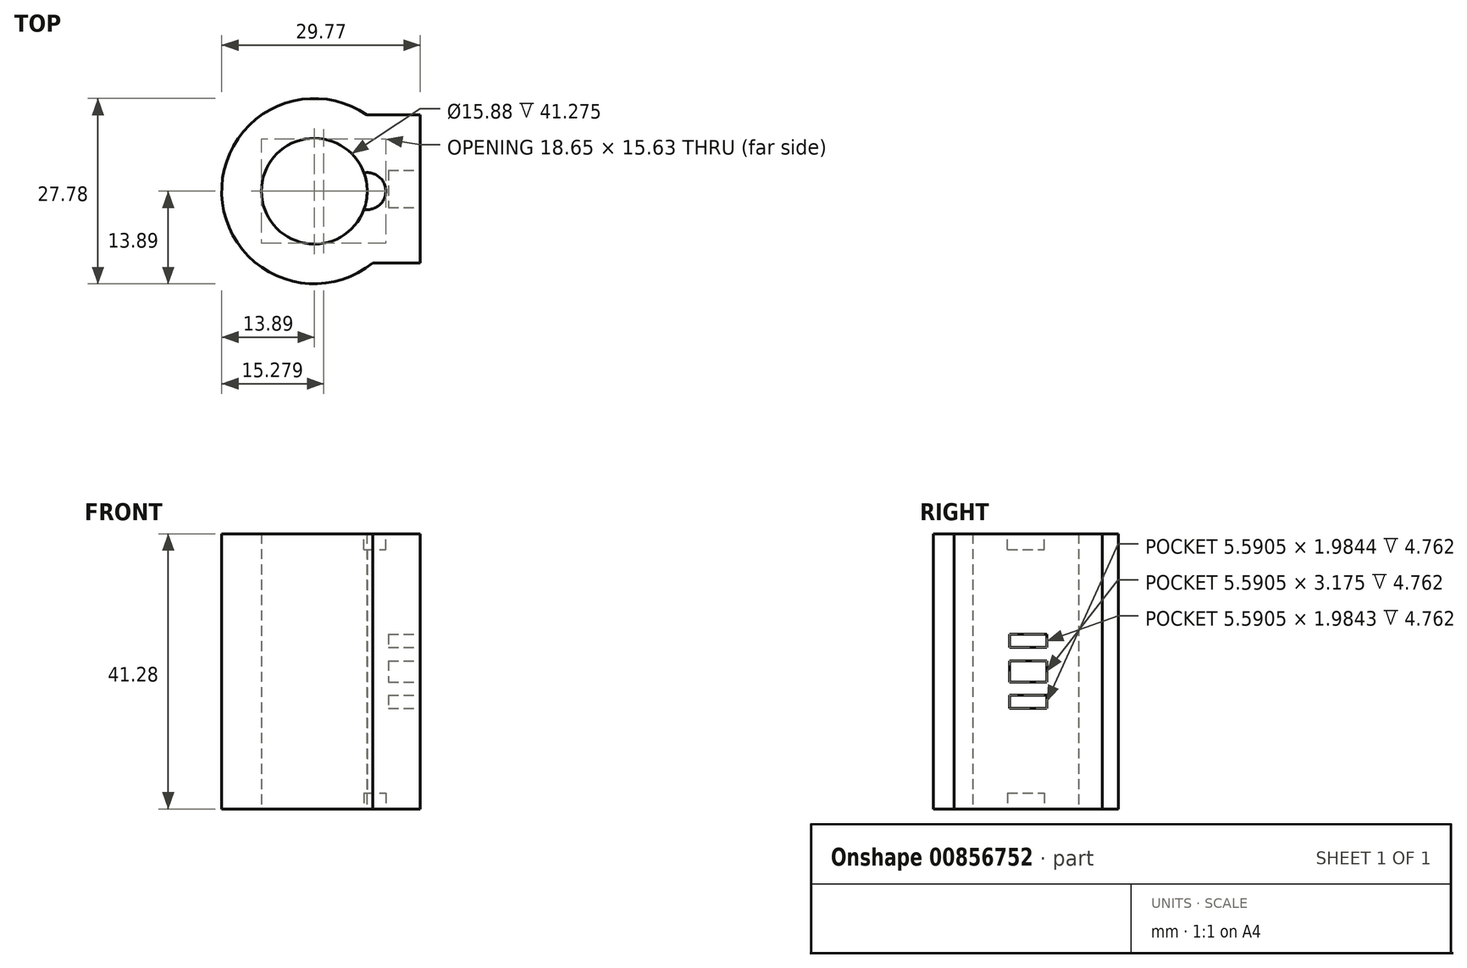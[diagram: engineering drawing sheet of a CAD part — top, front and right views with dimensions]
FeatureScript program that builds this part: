
annotation { "Feature Type Name" : "Feature", "Feature Type Description" : "" }
export const myFeature = defineFeature(function(context is Context, id is Id, definition is map)
    precondition{}
    {
        {
            var Q0;
            Q0=qCreatedBy(makeId("Top.planeOp"),FACE);
            var sketch = newSketch(context, id + "F0", { "sketchPlane" : qUnion([Q0])});
            skCircle(sketch, "E0", {"center": v(0, 0) * mm, "radius": 13.9 * mm});
            skCircle(sketch, "E1", {"center": v(0, 0) * mm, "radius": 7.94 * mm});
            skLineSegment(sketch, "E2", {"start": v(7.88, 11.44) * mm, "end": v(15.88, 11.44) * mm});
            skLineSegment(sketch, "E3", {"start": v(15.88, 11.44) * mm, "end": v(15.88, -10.79) * mm});
            skLineSegment(sketch, "E4", {"start": v(15.88, -10.79) * mm, "end": v(8.75, -10.79) * mm});
            skLineSegment(sketch, "E5", {"start": v(15.88, 0.33) * mm, "end": v(49.03, 0.33) * mm});
            skSolve(sketch);
        }
        {
            var Q0;
            Q0=qCreatedBy(makeId("Top.planeOp"),FACE);
            var sketch = newSketch(context, id + "F1", { "sketchPlane" : qUnion([Q0])});
            skCircle(sketch, "E6", {"center": v(0, 0) * mm, "radius": 13.9 * mm});
            skCircle(sketch, "E7", {"center": v(0, 0) * mm, "radius": 7.94 * mm});
            skLineSegment(sketch, "E8", {"start": v(8.33, 11.11) * mm, "end": v(15.88, 11.11) * mm});
            skLineSegment(sketch, "E9", {"start": v(15.88, 11.11) * mm, "end": v(15.88, -11.11) * mm});
            skLineSegment(sketch, "E10", {"start": v(15.88, -11.11) * mm, "end": v(8.33, -11.11) * mm});
            skLineSegment(sketch, "E11", {"start": v(15.88, 0) * mm, "end": v(63.04, 0) * mm, "construction": true});
            skLineSegment(sketch, "E12", {"start": v(-8.33, -11.11) * mm, "end": v(-13.56, -11.11) * mm});
            skPoint(sketch, "E12.startSnap0", {"position": v(12.1, -11.11) * mm});
            skLineSegment(sketch, "E13", {"start": v(-13.56, -11.11) * mm, "end": v(-13.56, -3.03) * mm});
            skCircle(sketch, "E14", {"center": v(7.94, 0) * mm, "radius": 2.78 * mm});
            skSolve(sketch);
        }
        {
            var Q0;
            {var subQ0=sQuery(id+"F1.wireOp",EDGE,"E6");var subQ1=makeQuery(id+"F1.imprint","INTERSECT",VERTEX,{"derivedFrom":[subQ0,sQuery(id+"F1.wireOp",EDGE,"E8")]});Q0=makeQuery(id+"F1.imprint","IMPRINT",FACE,{"disambiguationData":[TD([[makeQuery(id+"F1.imprint","IMPRINT",EDGE,{"disambiguationData":[TD([[subQ1,-1.0]])],"derivedFrom":subQ0}),1.0]])]});}
            var Q1;
            {var subQ0=sQuery(id+"F1.wireOp",EDGE,"E14");var subQ1=sQuery(id+"F1.wireOp",EDGE,"E7");var subQ2=makeQuery(id+"F1.imprint","INTERSECT",VERTEX,{"disambiguationData":[OD(0.0)],"derivedFrom":[subQ1,subQ0]});Q1=makeQuery(id+"F1.imprint","IMPRINT",FACE,{"disambiguationData":[TD([[makeQuery(id+"F1.imprint","IMPRINT",EDGE,{"disambiguationData":[TD([[subQ2,-1.0]])],"derivedFrom":subQ1}),-1.0]])]});}
            extrude(context, id + "F2", {"entities" : qUnion([Q0, Q1]), "depth" : 41.27 * mm, "offsetDistance" : 25.4 * mm});
        }
        {
            var Q0;
            {var subQ3=sQuery(id+"F0.wireOp",EDGE,"E2");Q0=makeQuery(id+"F0.imprint","IMPRINT",FACE,{"disambiguationData":[TD([[makeQuery(id+"F0.imprint","IMPRINT",EDGE,{"derivedFrom":subQ3}),-1.0]])]});}
            extrude(context, id + "F3", {"entities" : qUnion([Q0]), "operationType" : NewBodyOperationType.ADD, "depth" : 41.27 * mm, "offsetDistance" : 25.4 * mm});
        }
        {
            var Q0;
            Q0=makeQuery(id+"F3.opExtrude","SWEPT_FACE",FACE,{"disambiguationData":[OSD([sQuery(id+"F0.wireOp",EDGE,"E3")])]});
            var sketch = newSketch(context, id + "F4", { "sketchPlane" : qUnion([Q0])});
            skLineSegment(sketch, "E15", {"start": v(11.44, 20.64) * mm, "end": v(-10.79, 20.64) * mm, "construction": true});
            skLineSegment(sketch, "E16.bottom", {"start": v(3.12, 22.23) * mm, "end": v(-2.47, 22.23) * mm});
            skLineSegment(sketch, "E16.top", {"start": v(3.12, 19.05) * mm, "end": v(-2.47, 19.05) * mm});
            skLineSegment(sketch, "E16.left", {"start": v(3.12, 22.23) * mm, "end": v(3.12, 19.05) * mm});
            skLineSegment(sketch, "E16.right", {"start": v(-2.47, 22.23) * mm, "end": v(-2.47, 19.05) * mm});
            skLineSegment(sketch, "E17.bottom", {"start": v(3.12, 26.2) * mm, "end": v(-2.47, 26.2) * mm});
            skLineSegment(sketch, "E17.top", {"start": v(3.12, 24.2) * mm, "end": v(-2.47, 24.2) * mm});
            skLineSegment(sketch, "E17.left", {"start": v(3.12, 26.2) * mm, "end": v(3.12, 24.2) * mm});
            skLineSegment(sketch, "E17.right", {"start": v(-2.47, 26.2) * mm, "end": v(-2.47, 24.2) * mm});
            skLineSegment(sketch, "E18.bottom", {"start": v(3.12, 17.07) * mm, "end": v(-2.47, 17.07) * mm});
            skLineSegment(sketch, "E18.top", {"start": v(3.12, 15.08) * mm, "end": v(-2.47, 15.08) * mm});
            skLineSegment(sketch, "E18.left", {"start": v(3.12, 17.07) * mm, "end": v(3.12, 15.08) * mm});
            skLineSegment(sketch, "E18.right", {"start": v(-2.47, 17.07) * mm, "end": v(-2.47, 15.08) * mm});
            skLineSegment(sketch, "E19", {"start": v(0.33, 30.05) * mm, "end": v(0.33, 10.65) * mm, "construction": true});
            skPoint(sketch, "E19.startSnap0", {"position": v(0.33, 26.2) * mm});
            skLineSegment(sketch, "E20", {"start": v(0.33, 29.51) * mm, "end": v(0.33, 6.83) * mm, "construction": true});
            skPoint(sketch, "E20.startSnap0", {"position": v(0.33, 20.64) * mm});
            skLineSegment(sketch, "E21", {"start": v(3.12, 20.64) * mm, "end": v(-2.47, 20.64) * mm, "construction": true});
            skLineSegment(sketch, "E22", {"start": v(-1.53, 24.2) * mm, "end": v(-1.53, 22.23) * mm, "construction": true});
            skLineSegment(sketch, "E23", {"start": v(-1.53, 19.05) * mm, "end": v(-1.53, 17.07) * mm, "construction": true});
            skSolve(sketch);
        }
        {
            var Q0;
            Q0=makeQuery(id+"F4.imprint","IMPRINT",FACE,{"disambiguationData":[TD([[makeQuery(id+"F4.imprint","IMPRINT",EDGE,{"derivedFrom":sQuery(id+"F4.wireOp",EDGE,"E17.bottom")}),1.0]])]});
            var Q1;
            Q1=makeQuery(id+"F4.imprint","IMPRINT",FACE,{"disambiguationData":[TD([[makeQuery(id+"F4.imprint","IMPRINT",EDGE,{"derivedFrom":sQuery(id+"F4.wireOp",EDGE,"E16.bottom")}),1.0]])]});
            var Q2;
            Q2=makeQuery(id+"F4.imprint","IMPRINT",FACE,{"disambiguationData":[TD([[makeQuery(id+"F4.imprint","IMPRINT",EDGE,{"derivedFrom":sQuery(id+"F4.wireOp",EDGE,"E18.bottom")}),1.0]])]});
            extrude(context, id + "F5", {"entities" : qUnion([Q0, Q1, Q2]), "operationType" : NewBodyOperationType.REMOVE, "oppositeDirection" : true, "depth" : 4.76 * mm, "offsetDistance" : 25.4 * mm});
        }
        {
            var Q0;
            Q0=makeQuery(id+"F3.boolean.opBoolean","MERGE",FACE,{"derivedFrom":[makeQuery(id+"F2.opExtrude","CAP_FACE",FACE,{"disambiguationData":[OSD([sQuery(id+"F1.wireOp",EDGE,"E6"),sQuery(id+"F1.wireOp",EDGE,"E7")])],"isStart":false}),makeQuery(id+"F3.opExtrude","CAP_FACE",FACE,{"disambiguationData":[OSD([sQuery(id+"F0.wireOp",EDGE,"E0"),sQuery(id+"F0.wireOp",EDGE,"E2"),sQuery(id+"F0.wireOp",EDGE,"E3"),sQuery(id+"F0.wireOp",EDGE,"E4")])],"isStart":false})]});
            var sketch = newSketch(context, id + "F6", { "sketchPlane" : qUnion([Q0])});
            skCircle(sketch, "E24", {"center": v(7.94, 0) * mm, "radius": 2.78 * mm});
            skSolve(sketch);
        }
        {
            var Q0;
            {var subQ0=sQuery(id+"F6.wireOp",EDGE,"E24");var subQ1=makeQuery(id+"F2.opExtrude","CAP_EDGE",EDGE,{"disambiguationData":[OSD([sQuery(id+"F1.wireOp",EDGE,"E7")])],"isStart":false});var subQ2=makeQuery(id+"F6.imprint","INTERSECT",VERTEX,{"disambiguationData":[OD(0.0)],"derivedFrom":[subQ1,subQ0]});Q0=makeQuery(id+"F6.imprint","IMPRINT",FACE,{"disambiguationData":[TD([[makeQuery(id+"F6.imprint","IMPRINT",EDGE,{"disambiguationData":[TD([[subQ2,-1.0]])],"derivedFrom":subQ0}),1.0]])]});}
            extrude(context, id + "F7", {"entities" : qUnion([Q0]), "operationType" : NewBodyOperationType.REMOVE, "oppositeDirection" : true, "depth" : 2.38 * mm, "offsetDistance" : 25.4 * mm});
        }
        {
            var Q0;
            {var subQ0=sQuery(id+"F1.wireOp",EDGE,"E14");var subQ1=sQuery(id+"F1.wireOp",EDGE,"E7");var subQ2=makeQuery(id+"F1.imprint","INTERSECT",VERTEX,{"disambiguationData":[OD(0.0)],"derivedFrom":[subQ1,subQ0]});Q0=makeQuery(id+"F1.imprint","IMPRINT",FACE,{"disambiguationData":[TD([[makeQuery(id+"F1.imprint","IMPRINT",EDGE,{"disambiguationData":[TD([[subQ2,-1.0]])],"derivedFrom":subQ1}),-1.0]])]});}
            extrude(context, id + "F8", {"entities" : qUnion([Q0]), "operationType" : NewBodyOperationType.REMOVE, "depth" : 2.38 * mm, "offsetDistance" : 25.4 * mm});
        }
    });
